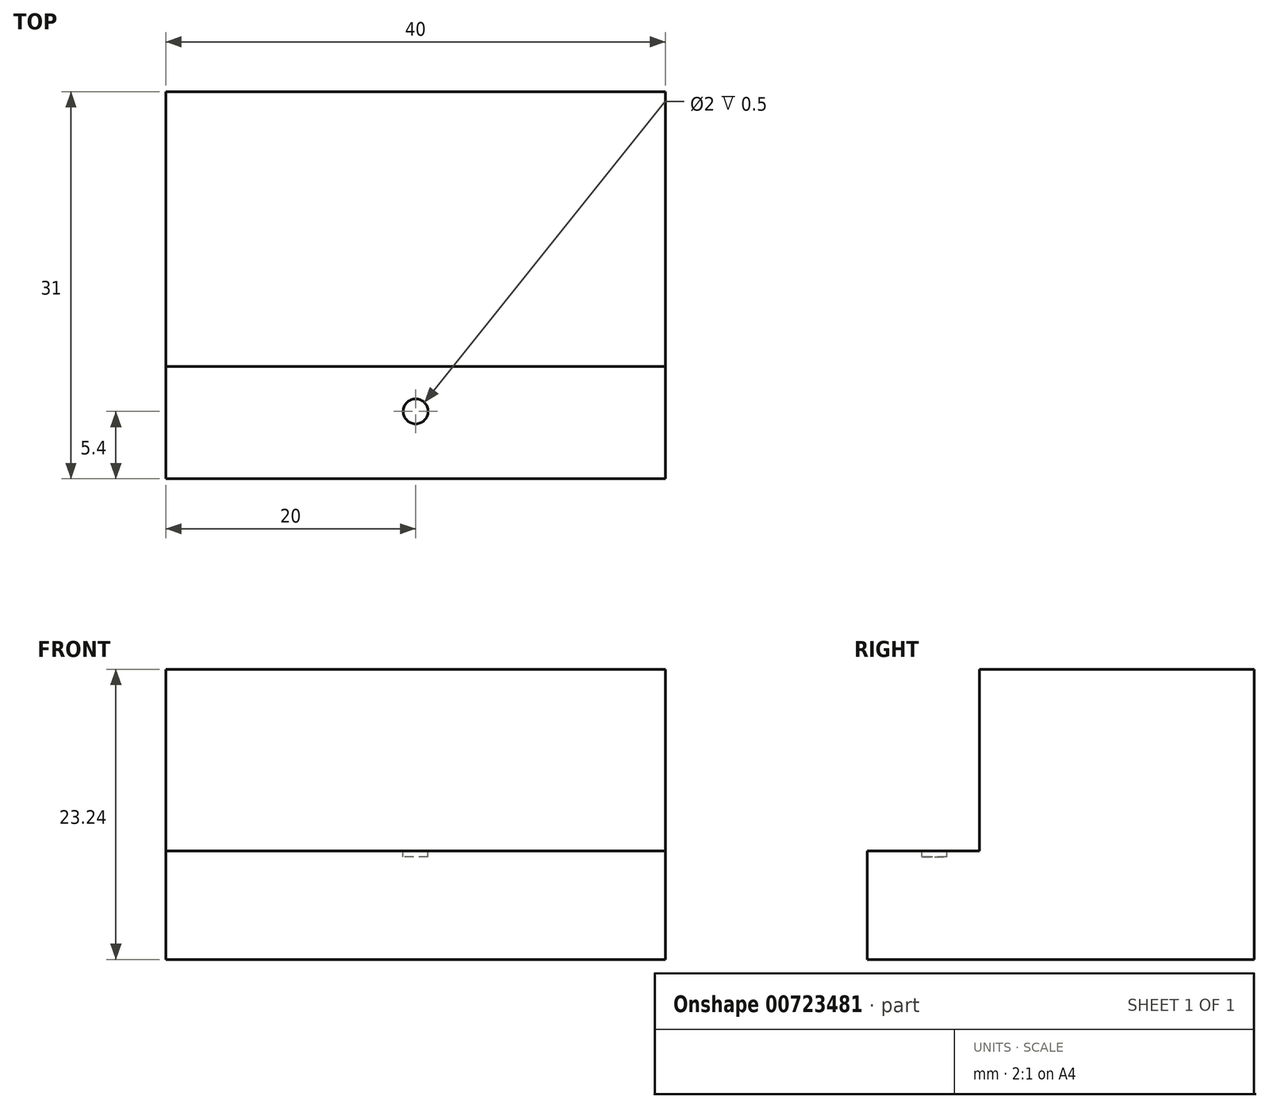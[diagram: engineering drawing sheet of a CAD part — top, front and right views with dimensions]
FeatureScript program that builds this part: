
annotation { "Feature Type Name" : "Feature", "Feature Type Description" : "" }
export const myFeature = defineFeature(function(context is Context, id is Id, definition is map)
    precondition{}
    {
        {
            var Q0;
            Q0=qCreatedBy(makeId("Top.planeOp"),FACE);
            var sketch = newSketch(context, id + "F0", { "sketchPlane" : qUnion([Q0])});
            skLineSegment(sketch, "E0.bottom", {"start": v(20, 15.5) * mm, "end": v(-20, 15.5) * mm});
            skLineSegment(sketch, "E0.top", {"start": v(20, -15.5) * mm, "end": v(-20, -15.5) * mm});
            skLineSegment(sketch, "E0.left", {"start": v(20, 15.5) * mm, "end": v(20, -15.5) * mm});
            skLineSegment(sketch, "E0.right", {"start": v(-20, 15.5) * mm, "end": v(-20, -15.5) * mm});
            skPoint(sketch, "E0.middle", {"position": v(0, 0) * mm});
            skSolve(sketch);
        }
        {
            var Q0;
            Q0 = qSketchRegion(id + "F0", true);
            extrude(context, id + "F1", {"entities" : qUnion([Q0]), "depth" : 8.7 * mm, "offsetDistance" : 25 * mm});
        }
        {
            var Q0;
            Q0=makeQuery(id+"F1.opExtrude","CAP_FACE",FACE,{"disambiguationData":[OSD([sQuery(id+"F0.wireOp",EDGE,"E0.bottom"),sQuery(id+"F0.wireOp",EDGE,"E0.top"),sQuery(id+"F0.wireOp",EDGE,"E0.left"),sQuery(id+"F0.wireOp",EDGE,"E0.right")])],"isStart":false});
            var sketch = newSketch(context, id + "F2", { "sketchPlane" : qUnion([Q0])});
            skLineSegment(sketch, "E1.bottom", {"start": v(-20, 15.5) * mm, "end": v(20, 15.5) * mm});
            skLineSegment(sketch, "E1.top", {"start": v(-20, -6.5) * mm, "end": v(20, -6.5) * mm});
            skLineSegment(sketch, "E1.left", {"start": v(-20, 15.5) * mm, "end": v(-20, -6.5) * mm});
            skLineSegment(sketch, "E1.right", {"start": v(20, 15.5) * mm, "end": v(20, -6.5) * mm});
            skSolve(sketch);
        }
        {
            var Q0;
            Q0 = qSketchRegion(id + "F2", true);
            extrude(context, id + "F3", {"entities" : qUnion([Q0]), "operationType" : NewBodyOperationType.ADD, "depth" : (23.24 - 8.7) * mm, "offsetDistance" : 25 * mm});
        }
        {
            var Q0;
            Q0=makeQuery(id+"F1.opExtrude","CAP_FACE",FACE,{"disambiguationData":[OSD([sQuery(id+"F0.wireOp",EDGE,"E0.bottom"),sQuery(id+"F0.wireOp",EDGE,"E0.top"),sQuery(id+"F0.wireOp",EDGE,"E0.left"),sQuery(id+"F0.wireOp",EDGE,"E0.right")])],"isStart":false});
            var sketch = newSketch(context, id + "F4", { "sketchPlane" : qUnion([Q0])});
            skCircle(sketch, "E2", {"center": v(0, -10.1) * mm, "radius": 1 * mm});
            skPoint(sketch, "E2.centerSnap0", {"position": v(0, -15.5) * mm});
            skSolve(sketch);
        }
        {
            var Q0;
            Q0 = qSketchRegion(id + "F4", true);
            extrude(context, id + "F5", {"entities" : qUnion([Q0]), "operationType" : NewBodyOperationType.REMOVE, "oppositeDirection" : true, "depth" : 0.5 * mm, "offsetDistance" : 25 * mm});
        }
    });
